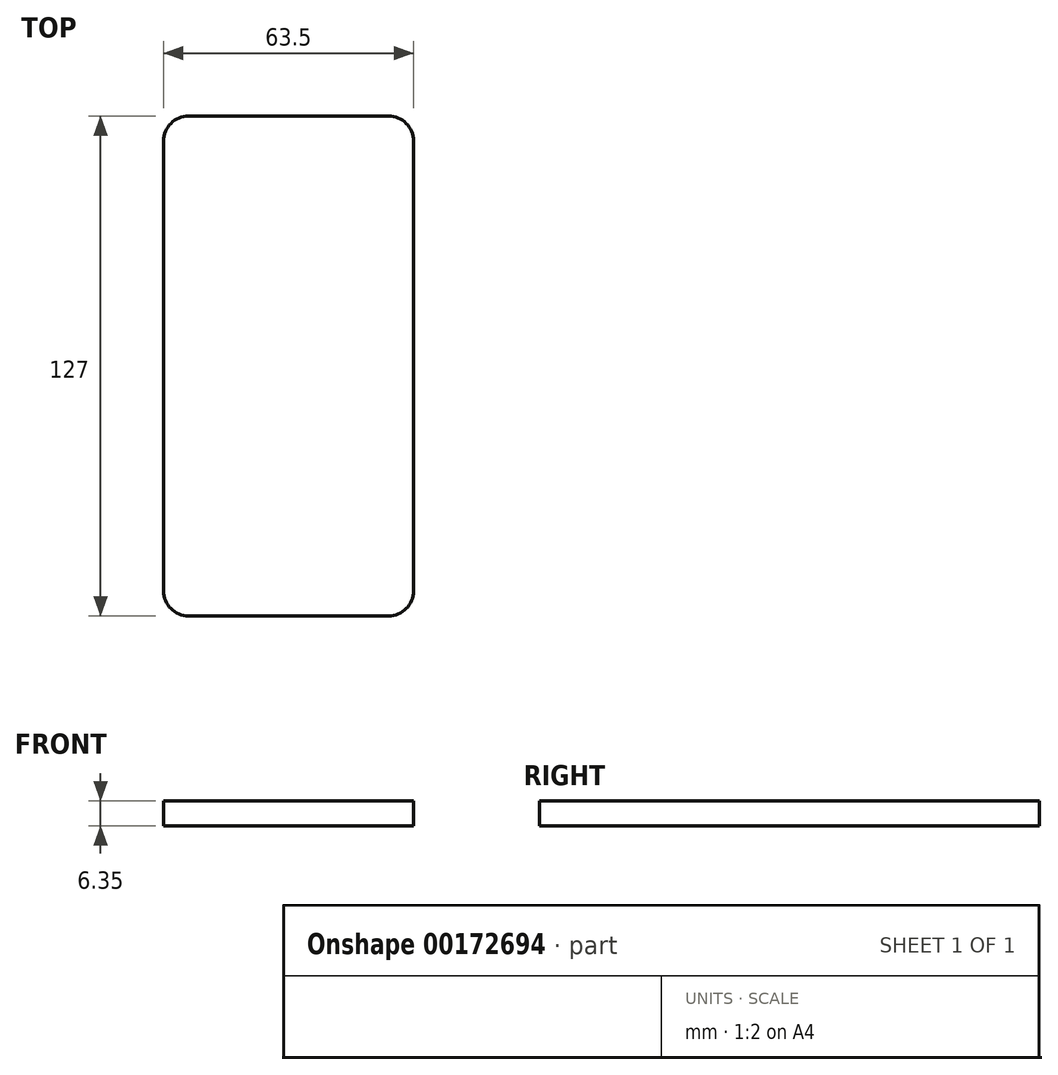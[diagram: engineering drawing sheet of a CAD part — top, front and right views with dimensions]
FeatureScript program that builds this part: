
annotation { "Feature Type Name" : "Feature", "Feature Type Description" : "" }
export const myFeature = defineFeature(function(context is Context, id is Id, definition is map)
    precondition{}
    {
        {
            var Q0;
            Q0=qCreatedBy(makeId("Top.planeOp"),FACE);
            var sketch = newSketch(context, id + "F0", { "sketchPlane" : qUnion([Q0])});
            skLineSegment(sketch, "E0", {"start": v(-54.23, 56.44) * mm, "end": v(-54.23, -57.86) * mm});
            skLineSegment(sketch, "E1", {"start": v(-47.88, -64.21) * mm, "end": v(2.92, -64.21) * mm});
            skLineSegment(sketch, "E2", {"start": v(9.27, -57.86) * mm, "end": v(9.27, 56.44) * mm});
            skLineSegment(sketch, "E3", {"start": v(-47.88, 62.79) * mm, "end": v(2.92, 62.79) * mm});
            skPoint(sketch, "E4.visualSharp", {"position": v(-54.23, 62.79) * mm});
            skArc(sketch, "E4.filletArc", {"start": v(-47.88, 62.79) * mm, "mid": v(-52.37, 60.93) * mm, "end": v(-54.23, 56.44) * mm});
            skPoint(sketch, "E5.visualSharp", {"position": v(9.27, 62.79) * mm});
            skArc(sketch, "E5.filletArc", {"start": v(9.27, 56.44) * mm, "mid": v(7.41, 60.93) * mm, "end": v(2.92, 62.79) * mm});
            skPoint(sketch, "E6.visualSharp", {"position": v(-54.23, -64.21) * mm});
            skArc(sketch, "E6.filletArc", {"start": v(-54.23, -57.86) * mm, "mid": v(-52.37, -62.35) * mm, "end": v(-47.88, -64.21) * mm});
            skPoint(sketch, "E7.visualSharp", {"position": v(9.27, -64.21) * mm});
            skArc(sketch, "E7.filletArc", {"start": v(2.92, -64.21) * mm, "mid": v(7.41, -62.35) * mm, "end": v(9.27, -57.86) * mm});
            skSolve(sketch);
        }
        {
            var Q0;
            Q0 = qSketchRegion(id + "F0", true);
            extrude(context, id + "F1", {"entities" : qUnion([Q0]), "depth" : 6.35 * mm});
        }
    });
